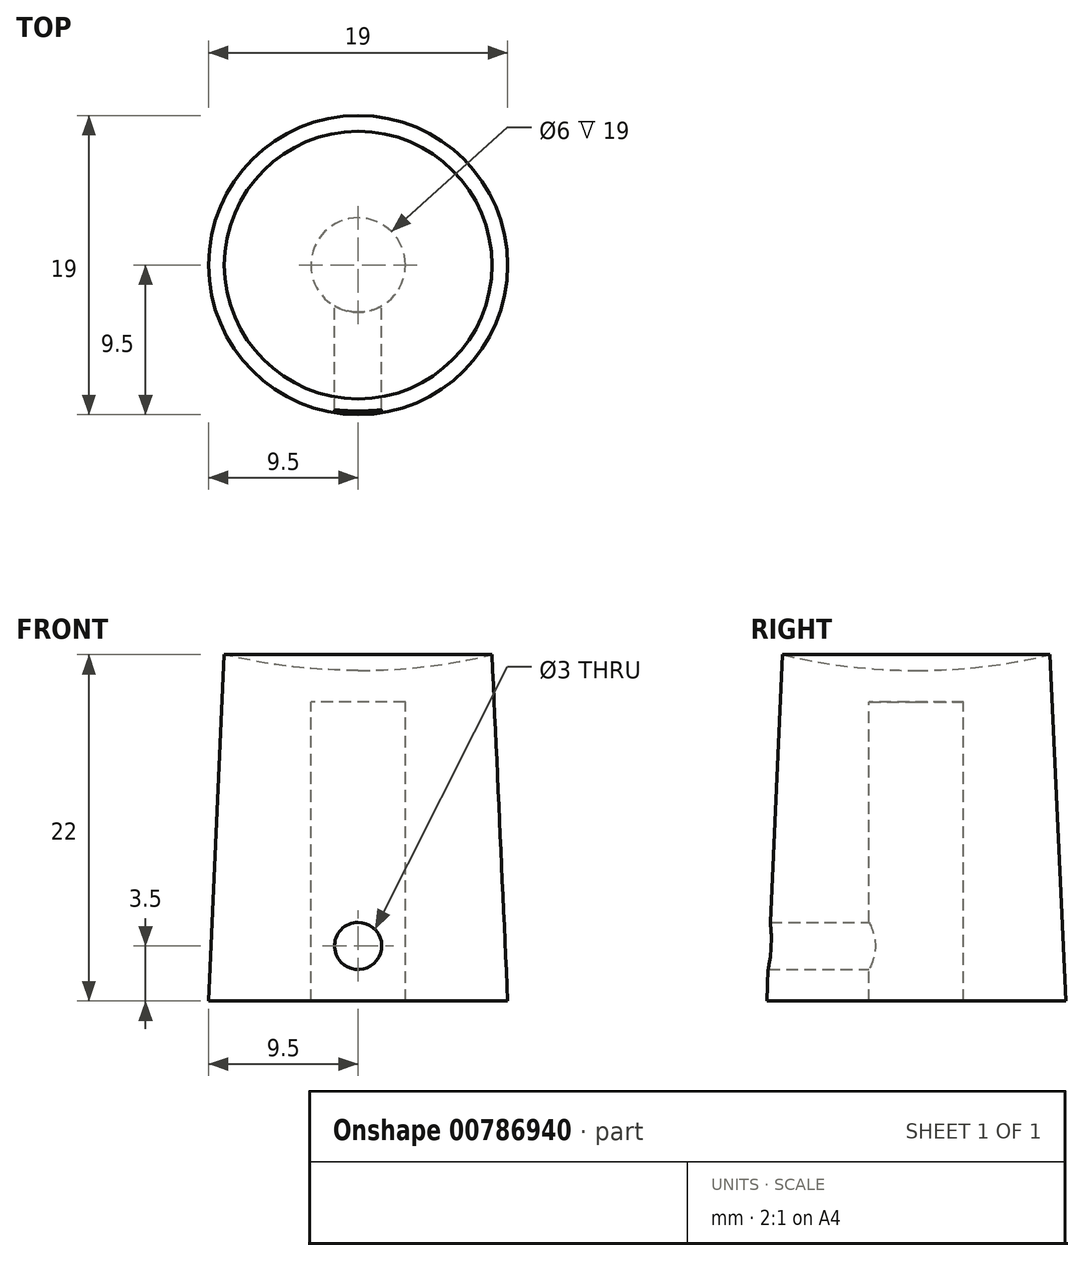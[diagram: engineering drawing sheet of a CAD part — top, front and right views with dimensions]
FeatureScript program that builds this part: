
annotation { "Feature Type Name" : "Feature", "Feature Type Description" : "" }
export const myFeature = defineFeature(function(context is Context, id is Id, definition is map)
    precondition{}
    {
        {
            var Q0;
            Q0=qCreatedBy(makeId("Front.planeOp"),FACE);
            var sketch = newSketch(context, id + "F0", { "sketchPlane" : qUnion([Q0])});
            skLineSegment(sketch, "E0", {"start": v(-3, 0) * mm, "end": v(-3, 19) * mm});
            skLineSegment(sketch, "E1", {"start": v(-3, 0) * mm, "end": v(-9.5, 0) * mm});
            skLineSegment(sketch, "E2", {"start": v(-9.5, 0) * mm, "end": v(-8.5, 22) * mm});
            skArc(sketch, "E3", {"start": v(-8.5, 22) * mm, "mid": v(-4.28, 21.25) * mm, "end": v(0, 21) * mm});
            skLineSegment(sketch, "E4", {"start": v(0, 21) * mm, "end": v(0, 19) * mm});
            skLineSegment(sketch, "E5", {"start": v(0, 19) * mm, "end": v(-3, 19) * mm});
            skSolve(sketch);
        }
        {
            var Q0;
            Q0=makeQuery(id+"F0.imprint","IMPRINT",FACE,{"disambiguationData":[TD([[makeQuery(id+"F0.imprint","IMPRINT",EDGE,{"derivedFrom":sQuery(id+"F0.wireOp",EDGE,"E0")}),1.0]])]});
            var Q1;
            Q1=sQuery(id+"F0.wireOp",EDGE,"E4");
            revolve(context, id + "F1", {"surfaceOperationType" : NewSurfaceOperationType.NEW, "entities" : qUnion([Q0]), "axis" : qUnion([Q1]), "revolveType" : RevolveType.FULL});
        }
        {
            var Q0;
            Q0=qCreatedBy(makeId("Front.planeOp"),FACE);
            var sketch = newSketch(context, id + "F2", { "sketchPlane" : qUnion([Q0])});
            skCircle(sketch, "E6", {"center": v(0, 3.5) * mm, "radius": 1.5 * mm});
            skSolve(sketch);
        }
        {
            var Q0;
            Q0 = qSketchRegion(id + "F2", true);
            extrude(context, id + "F3", {"entities" : qUnion([Q0]), "operationType" : NewBodyOperationType.REMOVE, "endBound" : BoundingType.THROUGH_ALL, "depth" : 25 * mm, "offsetDistance" : 25 * mm});
        }
    });
